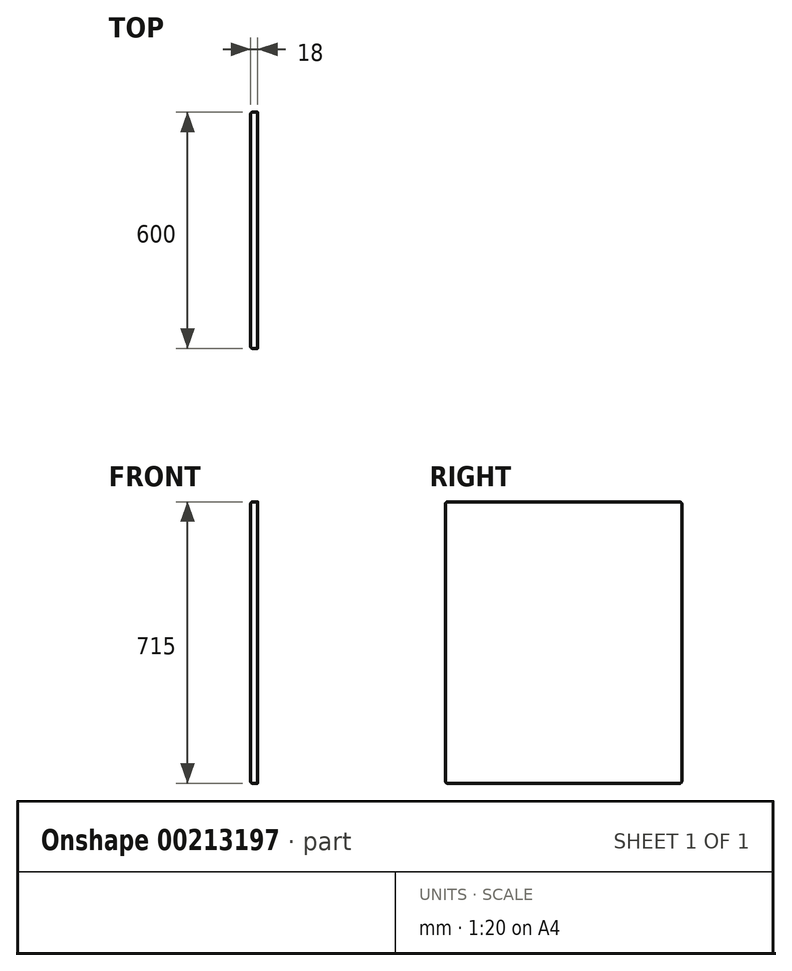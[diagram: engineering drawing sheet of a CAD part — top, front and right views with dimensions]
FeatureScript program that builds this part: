
annotation { "Feature Type Name" : "Feature", "Feature Type Description" : "" }
export const myFeature = defineFeature(function(context is Context, id is Id, definition is map)
    precondition{}
    {
        {
            var Q0;
            Q0=qCreatedBy(makeId("Right.planeOp"),FACE);
            var sketch = newSketch(context, id + "F0", { "sketchPlane" : qUnion([Q0])});
            skLineSegment(sketch, "E0.bottom", {"start": v(-300, 357.5) * mm, "end": v(300, 357.5) * mm});
            skLineSegment(sketch, "E0.top", {"start": v(-300, -357.5) * mm, "end": v(300, -357.5) * mm});
            skLineSegment(sketch, "E0.left", {"start": v(-300, 357.5) * mm, "end": v(-300, -357.5) * mm});
            skLineSegment(sketch, "E0.right", {"start": v(300, 357.5) * mm, "end": v(300, -357.5) * mm});
            skPoint(sketch, "E0.middle", {"position": v(0, 0) * mm});
            skSolve(sketch);
        }
        {
            var Q0;
            Q0=makeQuery(id+"F0.imprint","IMPRINT",FACE,{"disambiguationData":[TD([[makeQuery(id+"F0.imprint","IMPRINT",EDGE,{"derivedFrom":sQuery(id+"F0.wireOp",EDGE,"E0.bottom")}),-1.0]])]});
            extrude(context, id + "F1", {"entities" : qUnion([Q0]), "endBound" : BoundingType.SYMMETRIC, "depth" : 18 * mm});
        }
        {
            var Q0;
            Q0=makeQuery(id+"F1.opExtrude","CAP_FACE",FACE,{"disambiguationData":[OSD([sQuery(id+"F0.wireOp",EDGE,"E0.bottom"),sQuery(id+"F0.wireOp",EDGE,"E0.top"),sQuery(id+"F0.wireOp",EDGE,"E0.left"),sQuery(id+"F0.wireOp",EDGE,"E0.right")])],"isStart":true});
            var Q1;
            Q1=makeQuery(id+"F1.opExtrude","SWEPT_EDGE",EDGE,{"disambiguationData":[OSD([sQuery(id+"F0.wireOp",EDGE,"E0.bottom"),sQuery(id+"F0.wireOp",EDGE,"E0.right")])]});
            var Q2;
            Q2=makeQuery(id+"F1.opExtrude","SWEPT_EDGE",EDGE,{"disambiguationData":[OSD([sQuery(id+"F0.wireOp",EDGE,"E0.top"),sQuery(id+"F0.wireOp",EDGE,"E0.right")])]});
            var Q3;
            Q3=makeQuery(id+"F1.opExtrude","SWEPT_EDGE",EDGE,{"disambiguationData":[OSD([sQuery(id+"F0.wireOp",EDGE,"E0.top"),sQuery(id+"F0.wireOp",EDGE,"E0.left")])]});
            var Q4;
            Q4=makeQuery(id+"F1.opExtrude","SWEPT_EDGE",EDGE,{"disambiguationData":[OSD([sQuery(id+"F0.wireOp",EDGE,"E0.bottom"),sQuery(id+"F0.wireOp",EDGE,"E0.left")])]});
            fillet(context, id + "F2", {"entities" : qUnion([Q0, Q1, Q2, Q3, Q4]), "radius" : 5 * mm, "tangentPropagation" : true, "allowEdgeOverflow" : false});
        }
    });
